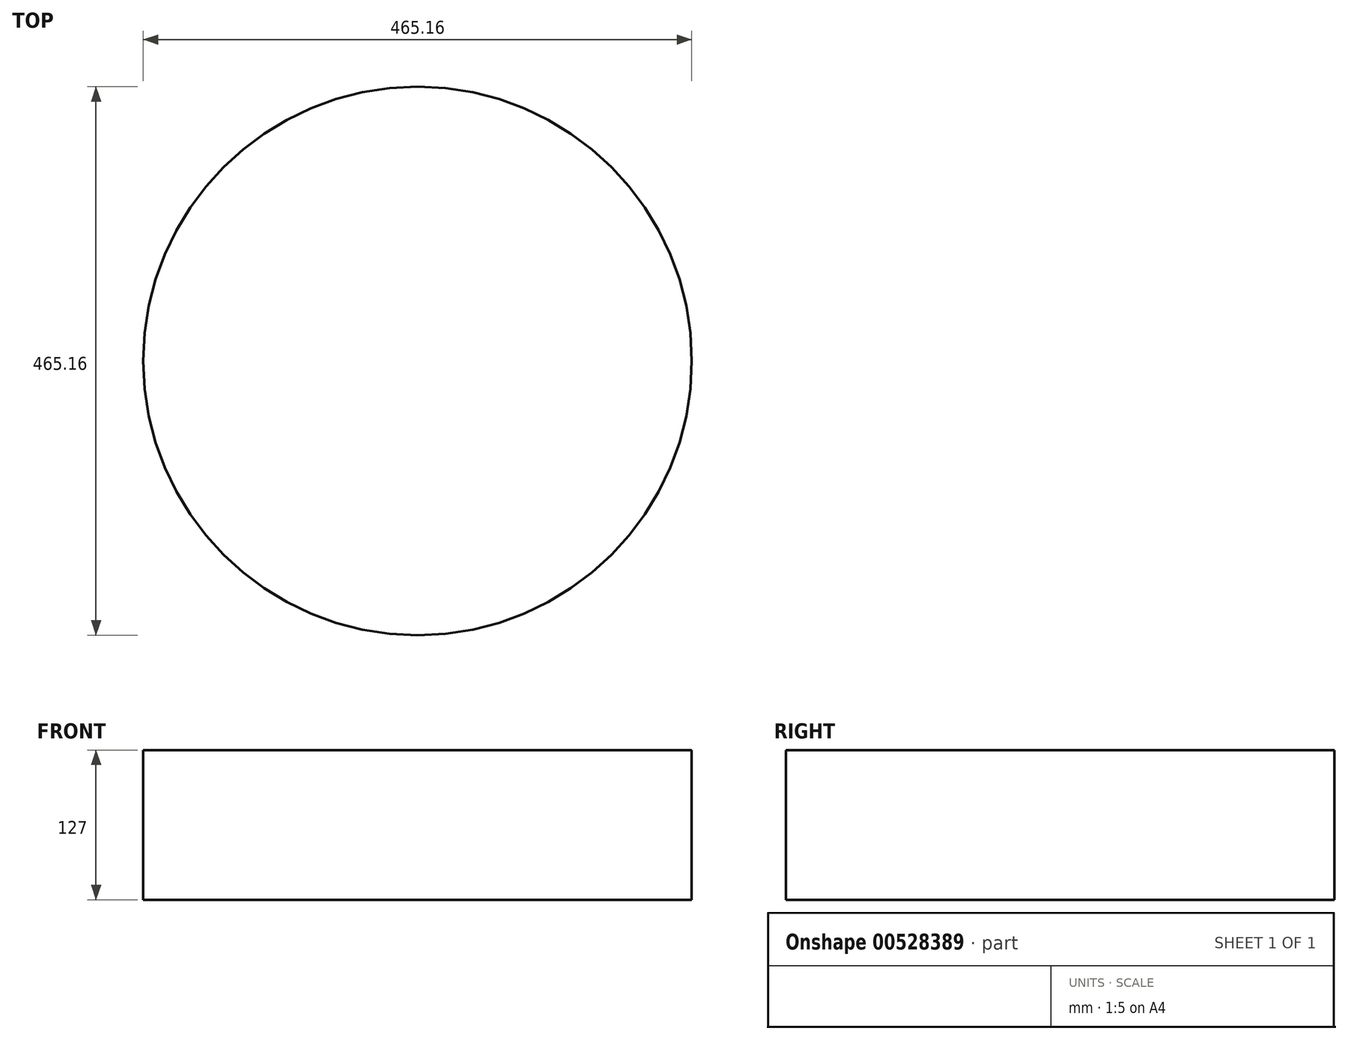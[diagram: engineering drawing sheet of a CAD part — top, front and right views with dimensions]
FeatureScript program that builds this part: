
annotation { "Feature Type Name" : "Feature", "Feature Type Description" : "" }
export const myFeature = defineFeature(function(context is Context, id is Id, definition is map)
    precondition{}
    {
        {
            var Q0;
            Q0=qCreatedBy(makeId("Top.planeOp"),FACE);
            var sketch = newSketch(context, id + "F0", { "sketchPlane" : qUnion([Q0])});
            skCircle(sketch, "E0", {"center": v(-175.46, 18.5) * mm, "radius": 232.58 * mm});
            skSolve(sketch);
        }
        {
            var Q0;
            Q0 = qSketchRegion(id + "F0", true);
            extrude(context, id + "F1", {"entities" : qUnion([Q0]), "depth" : 127 * mm, "offsetDistance" : 25.4 * mm});
        }
    });
